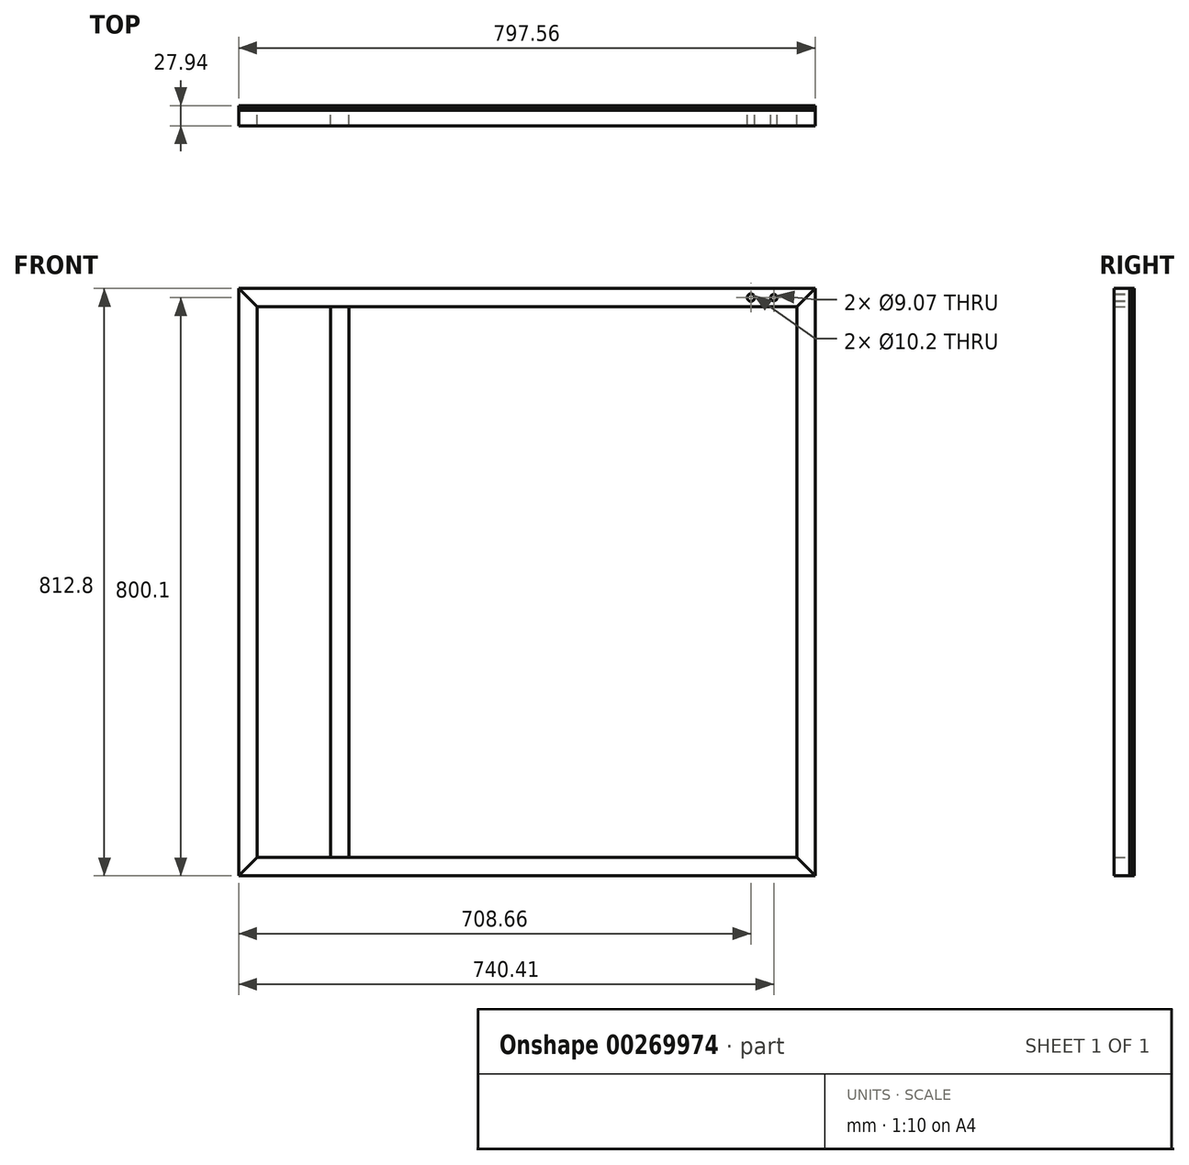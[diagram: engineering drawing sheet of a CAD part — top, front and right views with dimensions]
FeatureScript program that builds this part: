
annotation { "Feature Type Name" : "Feature", "Feature Type Description" : "" }
export const myFeature = defineFeature(function(context is Context, id is Id, definition is map)
    precondition{}
    {
        {
            var Q0;
            Q0=qCreatedBy(makeId("Front.planeOp"),FACE);
            var sketch = newSketch(context, id + "F0", { "sketchPlane" : qUnion([Q0])});
            skLineSegment(sketch, "E0", {"start": v(0, 0) * mm, "end": v(-25.4, -25.4) * mm});
            skLineSegment(sketch, "E1", {"start": v(-25.4, -25.4) * mm, "end": v(-25.4, -787.4) * mm});
            skLineSegment(sketch, "E2", {"start": v(-25.4, -787.4) * mm, "end": v(0, -812.8) * mm});
            skLineSegment(sketch, "E3", {"start": v(0, -812.8) * mm, "end": v(0, 0) * mm});
            skLineSegment(sketch, "E4", {"start": v(0, 0) * mm, "end": v(-797.56, 0) * mm});
            skLineSegment(sketch, "E5", {"start": v(-797.56, 0) * mm, "end": v(-772.16, -25.4) * mm});
            skLineSegment(sketch, "E6", {"start": v(-772.16, -25.4) * mm, "end": v(-25.4, -25.4) * mm});
            skLineSegment(sketch, "E7", {"start": v(-25.4, -787.4) * mm, "end": v(-772.16, -787.4) * mm});
            skLineSegment(sketch, "E8", {"start": v(-772.16, -787.4) * mm, "end": v(-797.56, -812.8) * mm});
            skLineSegment(sketch, "E9", {"start": v(-797.56, -812.8) * mm, "end": v(0, -812.8) * mm});
            skLineSegment(sketch, "E10", {"start": v(-797.56, 0) * mm, "end": v(-797.56, -812.8) * mm});
            skLineSegment(sketch, "E11", {"start": v(-772.16, -25.4) * mm, "end": v(-772.16, -787.4) * mm});
            skLineSegment(sketch, "E12.bottom", {"start": v(-797.56, 0) * mm, "end": v(0, 0) * mm});
            skLineSegment(sketch, "E12.right", {"start": v(0, 0) * mm, "end": v(0, -812.8) * mm});
            skLineSegment(sketch, "E13.bottom", {"start": v(-670.56, -25.4) * mm, "end": v(-645.16, -25.4) * mm});
            skLineSegment(sketch, "E13.top", {"start": v(-670.56, -787.4) * mm, "end": v(-645.16, -787.4) * mm});
            skLineSegment(sketch, "E13.left", {"start": v(-670.56, -25.4) * mm, "end": v(-670.56, -787.4) * mm});
            skLineSegment(sketch, "E13.right", {"start": v(-645.16, -25.4) * mm, "end": v(-645.16, -787.4) * mm});
            skCircle(sketch, "E14", {"center": v(-88.9, -12.7) * mm, "radius": 5.1 * mm});
            skPoint(sketch, "E14.centerSnap0", {"position": v(-12.7, -12.7) * mm});
            skCircle(sketch, "E15", {"center": v(-57.15, -12.7) * mm, "radius": 4.53 * mm});
            skSolve(sketch);
        }
        {
            var Q0;
            Q0=makeQuery(id+"F0.imprint","IMPRINT",FACE,{"disambiguationData":[TD([[makeQuery(id+"F0.imprint","IMPRINT",EDGE,{"derivedFrom":sQuery(id+"F0.wireOp",EDGE,"E0")}),1.0]])]});
            extrude(context, id + "F1", {"entities" : qUnion([Q0]), "depth" : 25.4 * mm, "offsetDistance" : 25.4 * mm});
        }
        {
            var Q0;
            Q0=makeQuery(id+"F0.imprint","IMPRINT",FACE,{"disambiguationData":[TD([[makeQuery(id+"F0.imprint","IMPRINT",EDGE,{"derivedFrom":sQuery(id+"F0.wireOp",EDGE,"E2")}),-1.0]])]});
            extrude(context, id + "F2", {"entities" : qUnion([Q0]), "depth" : 25.4 * mm, "offsetDistance" : 25.4 * mm});
        }
        {
            var Q0;
            Q0=makeQuery(id+"F0.imprint","IMPRINT",FACE,{"disambiguationData":[TD([[makeQuery(id+"F0.imprint","IMPRINT",EDGE,{"derivedFrom":sQuery(id+"F0.wireOp",EDGE,"E5")}),-1.0]])]});
            extrude(context, id + "F3", {"entities" : qUnion([Q0]), "depth" : 25.4 * mm, "offsetDistance" : 25.4 * mm});
        }
        {
            var Q0;
            Q0=makeQuery(id+"F0.imprint","IMPRINT",FACE,{"disambiguationData":[TD([[makeQuery(id+"F0.imprint","IMPRINT",EDGE,{"derivedFrom":sQuery(id+"F0.wireOp",EDGE,"E0")}),-1.0]])]});
            extrude(context, id + "F4", {"entities" : qUnion([Q0]), "depth" : 25.4 * mm, "offsetDistance" : 25.4 * mm});
        }
        {
            var Q0;
            {var subQ2=sQuery(id+"F0.wireOp",EDGE,"E13.left");Q0=makeQuery(id+"F0.imprint","IMPRINT",FACE,{"disambiguationData":[TD([[makeQuery(id+"F0.imprint","IMPRINT",EDGE,{"derivedFrom":subQ2}),1.0]])]});}
            extrude(context, id + "F5", {"entities" : qUnion([Q0]), "depth" : 25.4 * mm, "offsetDistance" : 25.4 * mm});
        }
        {
            var Q0;
            Q0=makeQuery(id+"F0.imprint","IMPRINT",FACE,{"disambiguationData":[TD([[makeQuery(id+"F0.imprint","IMPRINT",EDGE,{"derivedFrom":sQuery(id+"F0.wireOp",EDGE,"E5")}),-1.0]])]});
            var Q1;
            {var subQ4=sQuery(id+"F0.wireOp",EDGE,"E2");Q1=makeQuery(id+"F0.imprint","IMPRINT",FACE,{"disambiguationData":[TD([[makeQuery(id+"F0.imprint","IMPRINT",EDGE,{"derivedFrom":subQ4}),-1.0]])]});}
            var Q2;
            {var subQ0=sQuery(id+"F0.wireOp",EDGE,"E11");Q2=makeQuery(id+"F0.imprint","IMPRINT",FACE,{"disambiguationData":[TD([[makeQuery(id+"F0.imprint","IMPRINT",EDGE,{"derivedFrom":subQ0}),1.0]])]});}
            var Q3;
            {var subQ2=sQuery(id+"F0.wireOp",EDGE,"E13.left");Q3=makeQuery(id+"F0.imprint","IMPRINT",FACE,{"disambiguationData":[TD([[makeQuery(id+"F0.imprint","IMPRINT",EDGE,{"derivedFrom":subQ2}),1.0]])]});}
            var Q4;
            {var subQ0=sQuery(id+"F0.wireOp",EDGE,"E1");Q4=makeQuery(id+"F0.imprint","IMPRINT",FACE,{"disambiguationData":[TD([[makeQuery(id+"F0.imprint","IMPRINT",EDGE,{"derivedFrom":subQ0}),-1.0]])]});}
            var Q5;
            Q5=makeQuery(id+"F0.imprint","IMPRINT",FACE,{"disambiguationData":[TD([[makeQuery(id+"F0.imprint","IMPRINT",EDGE,{"derivedFrom":sQuery(id+"F0.wireOp",EDGE,"E0")}),1.0]])]});
            var Q6;
            {var subQ1=sQuery(id+"F0.wireOp",EDGE,"E0");Q6=makeQuery(id+"F0.imprint","IMPRINT",FACE,{"disambiguationData":[TD([[makeQuery(id+"F0.imprint","IMPRINT",EDGE,{"derivedFrom":subQ1}),-1.0]])]});}
            extrude(context, id + "F6", {"entities" : qUnion([Q0, Q1, Q2, Q3, Q4, Q5, Q6]), "depth" : 6.35 * mm, "offsetDistance" : 25.4 * mm});
        }
        {
            var Q0;
            Q0=makeQuery(id+"F6.opExtrude","SWEPT_BODY",BODY,{"disambiguationData":[OSD([sQuery(id+"F0.wireOp",EDGE,"E3"),sQuery(id+"F0.wireOp",EDGE,"E4"),sQuery(id+"F0.wireOp",EDGE,"E9"),sQuery(id+"F0.wireOp",EDGE,"E10")])]});
            transform(context, id + "F7", {"entities" : qUnion([Q0]), "transformType" : TransformType.TRANSLATION_3D, "dx" : 0 * mm, "dy" : 2.54 * mm, "dz" : 0 * mm, "makeCopy" : false});
        }
    });
